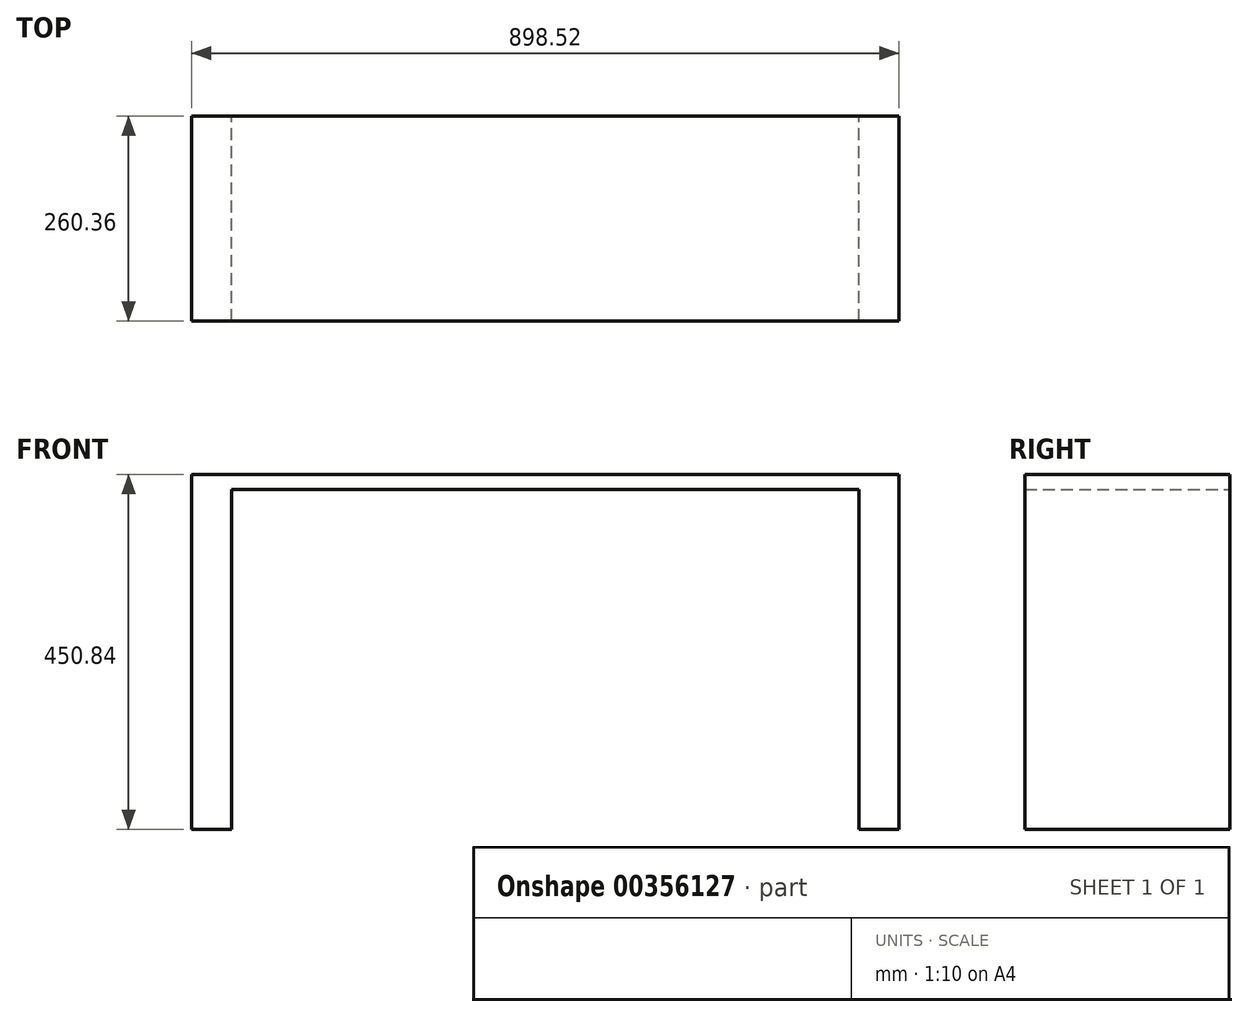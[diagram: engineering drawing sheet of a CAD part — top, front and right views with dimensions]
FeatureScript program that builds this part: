
annotation { "Feature Type Name" : "Feature", "Feature Type Description" : "" }
export const myFeature = defineFeature(function(context is Context, id is Id, definition is map)
    precondition{}
    {
        {
            var Q0;
            Q0=qCreatedBy(makeId("Front.planeOp"),FACE);
            var sketch = newSketch(context, id + "F0", { "sketchPlane" : qUnion([Q0])});
            skLineSegment(sketch, "E0.bottom", {"start": v(-449.26, -225.42) * mm, "end": v(-398.46, -225.42) * mm});
            skLineSegment(sketch, "E0.top", {"start": v(-449.26, 225.43) * mm, "end": v(449.26, 225.43) * mm});
            skLineSegment(sketch, "E0.left", {"start": v(-449.26, -225.42) * mm, "end": v(-449.26, 225.43) * mm});
            skLineSegment(sketch, "E0.right", {"start": v(449.26, -225.42) * mm, "end": v(449.26, 225.43) * mm});
            skPoint(sketch, "E0.middle", {"position": v(0, 0) * mm});
            skLineSegment(sketch, "E1.0", {"start": v(-398.46, -225.42) * mm, "end": v(-398.46, 206.38) * mm});
            skLineSegment(sketch, "E2.0", {"start": v(398.46, -225.42) * mm, "end": v(398.46, 206.38) * mm});
            skLineSegment(sketch, "E3.trimOffspring", {"start": v(398.46, -225.42) * mm, "end": v(449.26, -225.42) * mm});
            skLineSegment(sketch, "E4.0", {"start": v(-449.26, 206.38) * mm, "end": v(449.26, 206.38) * mm});
            skSolve(sketch);
        }
        {
            var Q0;
            {var subQ0=sQuery(id+"F0.wireOp",EDGE,"E0.bottom");Q0=makeQuery(id+"F0.imprint","IMPRINT",FACE,{"disambiguationData":[TD([[makeQuery(id+"F0.imprint","IMPRINT",EDGE,{"derivedFrom":subQ0}),1.0]])]});}
            var Q1;
            {var subQ5=sQuery(id+"F0.wireOp",EDGE,"E0.top");Q1=makeQuery(id+"F0.imprint","IMPRINT",FACE,{"disambiguationData":[TD([[makeQuery(id+"F0.imprint","IMPRINT",EDGE,{"derivedFrom":subQ5}),-1.0]])]});}
            var Q2;
            {var subQ4=sQuery(id+"F0.wireOp",EDGE,"E2.0");Q2=makeQuery(id+"F0.imprint","IMPRINT",FACE,{"disambiguationData":[TD([[makeQuery(id+"F0.imprint","IMPRINT",EDGE,{"derivedFrom":subQ4}),-1.0]])]});}
            extrude(context, id + "F1", {"entities" : qUnion([Q0, Q1, Q2]), "endBound" : BoundingType.SYMMETRIC, "depth" : 260.35 * mm});
        }
    });
